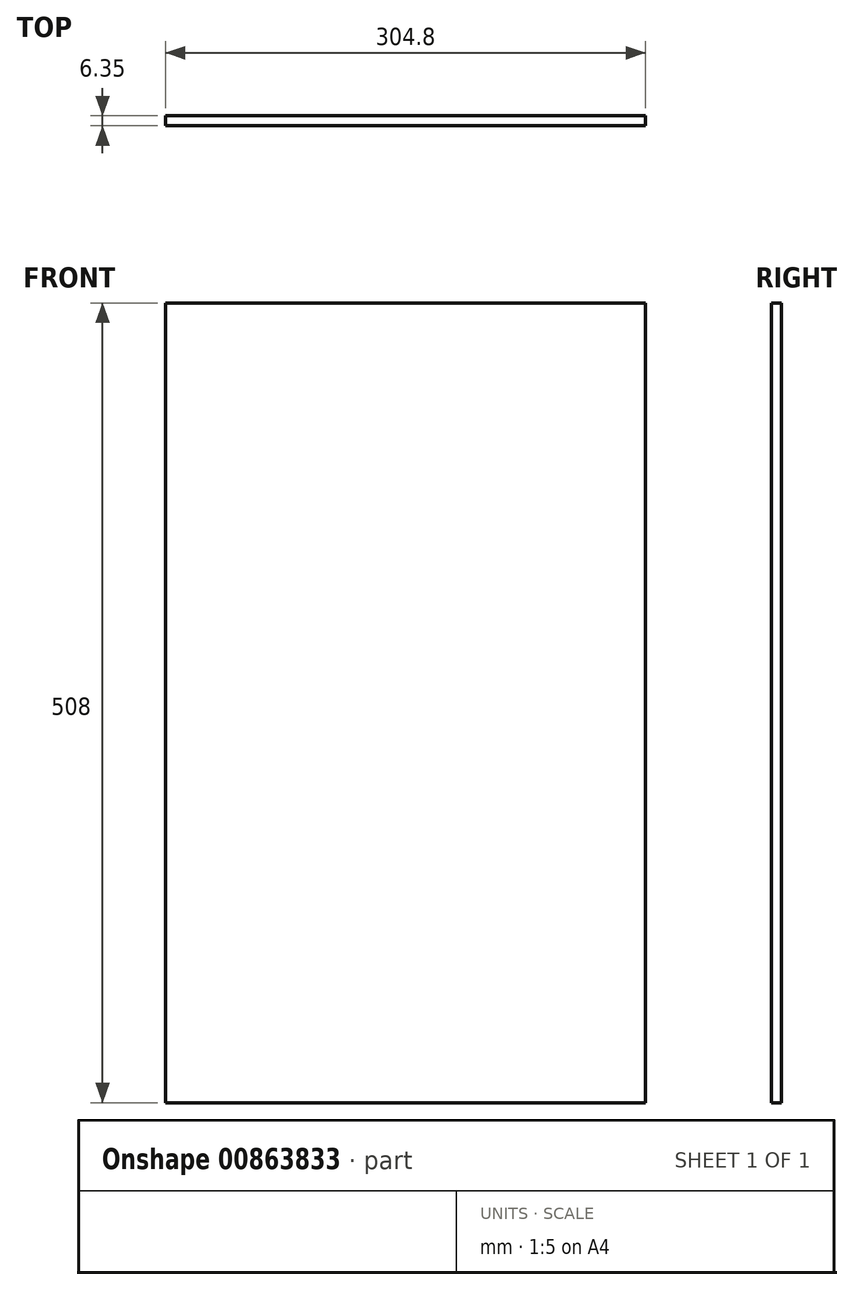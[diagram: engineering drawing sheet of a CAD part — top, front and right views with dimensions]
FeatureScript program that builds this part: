
annotation { "Feature Type Name" : "Feature", "Feature Type Description" : "" }
export const myFeature = defineFeature(function(context is Context, id is Id, definition is map)
    precondition{}
    {
        {
            var Q0;
            Q0=qCreatedBy(makeId("Front.planeOp"),FACE);
            var sketch = newSketch(context, id + "F0", { "sketchPlane" : qUnion([Q0])});
            skLineSegment(sketch, "E0.bottom", {"start": v(0, 0) * mm, "end": v(-304.8, 0) * mm});
            skLineSegment(sketch, "E0.top", {"start": v(0, 508) * mm, "end": v(-304.8, 508) * mm});
            skLineSegment(sketch, "E0.left", {"start": v(0, 0) * mm, "end": v(0, 508) * mm});
            skLineSegment(sketch, "E0.right", {"start": v(-304.8, 0) * mm, "end": v(-304.8, 508) * mm});
            skSolve(sketch);
        }
        {
            var Q0;
            Q0=qSketchRegion(id+"F0",true);
            extrude(context, id + "F1", {"entities" : qUnion([Q0]), "oppositeDirection" : true, "depth" : 6.35 * mm, "offsetDistance" : 25.4 * mm});
        }
    });
